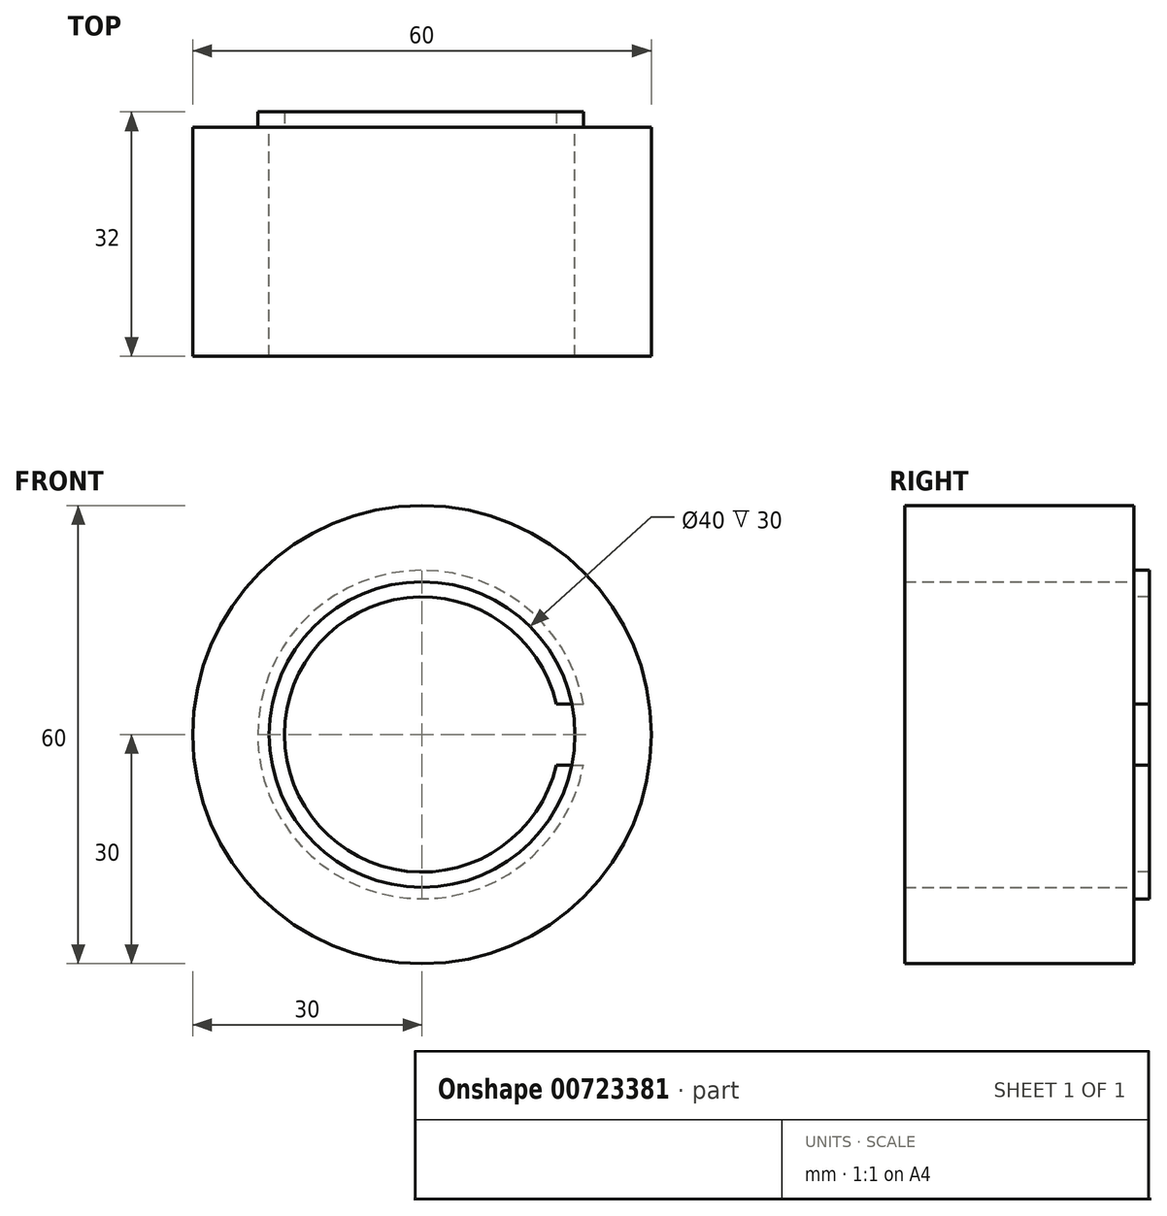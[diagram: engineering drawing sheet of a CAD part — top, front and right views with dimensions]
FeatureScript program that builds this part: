
annotation { "Feature Type Name" : "Feature", "Feature Type Description" : "" }
export const myFeature = defineFeature(function(context is Context, id is Id, definition is map)
    precondition{}
    {
        {
            var Q0;
            Q0=qCreatedBy(makeId("Front.planeOp"),FACE);
            var sketch = newSketch(context, id + "F0", { "sketchPlane" : qUnion([Q0])});
            skCircle(sketch, "E0", {"center": v(0, 0) * mm, "radius": 20 * mm});
            skCircle(sketch, "E1", {"center": v(0, 0) * mm, "radius": 30 * mm});
            skCircle(sketch, "E2", {"center": v(0, 0) * mm, "radius": 18 * mm});
            skLineSegment(sketch, "E3", {"start": v(17.55, 4) * mm, "end": v(19.6, 4) * mm});
            skLineSegment(sketch, "E4.MirrorCS", {"start": v(17.55, -4) * mm, "end": v(19.6, -4) * mm});
            skCircle(sketch, "E5", {"center": v(0, 0) * mm, "radius": 21.5 * mm});
            skLineSegment(sketch, "E6", {"start": v(19.6, 4) * mm, "end": v(21.12, 4) * mm});
            skLineSegment(sketch, "E7", {"start": v(19.6, -4) * mm, "end": v(21.12, -4) * mm});
            skSolve(sketch);
        }
        {
            var Q0;
            Q0=makeQuery(id+"F0.imprint","IMPRINT",FACE,{"disambiguationData":[TD([[makeQuery(id+"F0.imprint","IMPRINT",EDGE,{"derivedFrom":sQuery(id+"F0.wireOp",EDGE,"E0")}),-1.0]])]});
            var Q1;
            Q1=makeQuery(id+"F0.imprint","IMPRINT",FACE,{"disambiguationData":[TD([[makeQuery(id+"F0.imprint","IMPRINT",EDGE,{"derivedFrom":sQuery(id+"F0.wireOp",EDGE,"E1")}),1.0]])]});
            extrude(context, id + "F1", {"entities" : qUnion([Q0, Q1]), "depth" : 30 * mm, "offsetDistance" : 25 * mm});
        }
        {
            var Q0;
            {var subQ0=sQuery(id+"F0.wireOp",EDGE,"E3");Q0=makeQuery(id+"F0.imprint","IMPRINT",FACE,{"disambiguationData":[TD([[makeQuery(id+"F0.imprint","IMPRINT",EDGE,{"derivedFrom":subQ0}),1.0]])]});}
            var Q1;
            {var subQ0=sQuery(id+"F0.wireOp",EDGE,"E6");Q1=makeQuery(id+"F0.imprint","IMPRINT",FACE,{"disambiguationData":[TD([[makeQuery(id+"F0.imprint","IMPRINT",EDGE,{"derivedFrom":subQ0}),1.0]])]});}
            extrude(context, id + "F2", {"entities" : qUnion([Q0, Q1]), "oppositeDirection" : true, "depth" : 2 * mm, "offsetDistance" : 25 * mm});
        }
    });
